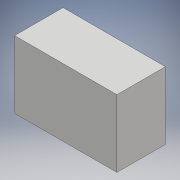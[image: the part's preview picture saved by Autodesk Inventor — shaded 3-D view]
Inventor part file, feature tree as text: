
AUTODESK INVENTOR PART (.ipt)
format: ipt  version: 2018.3 (Build 223284000, 284)  size: 85,504 bytes
history: native  units: mm
features: extrude x1, sketch x1
ambient origin geometry x8: Origin, YZ Plane, XZ Plane, XY Plane, X Axis, Y Axis, Z Axis, Center Point
bodies: Solid1 (feature_tree)
feature tree (2):
  extrude  "Extrusion1"  Depth=18.0mm
  sketch  "Sketch1"  dims[d0=38.0mm d1=18.0mm d2=25.0mm d3=0.0mm]
